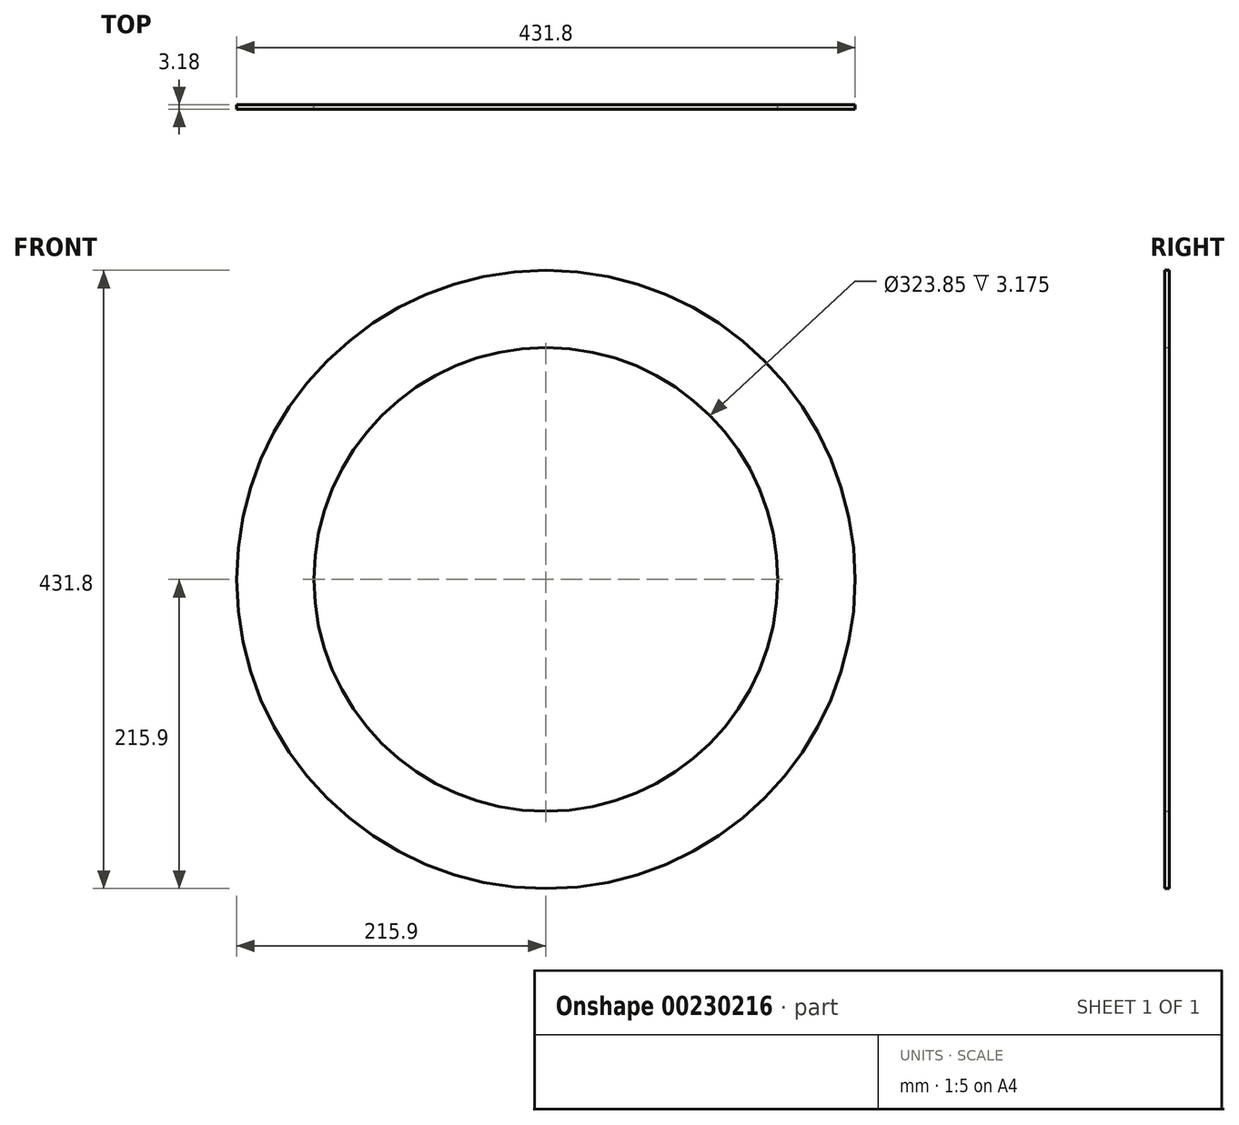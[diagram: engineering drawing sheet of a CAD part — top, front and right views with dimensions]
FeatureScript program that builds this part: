
annotation { "Feature Type Name" : "Feature", "Feature Type Description" : "" }
export const myFeature = defineFeature(function(context is Context, id is Id, definition is map)
    precondition{}
    {
        {
            var Q0;
            Q0=qCreatedBy(makeId("Front.planeOp"),FACE);
            var sketch = newSketch(context, id + "F0", { "sketchPlane" : qUnion([Q0])});
            skCircle(sketch, "E0", {"center": v(0, 0) * mm, "radius": 161.93 * mm});
            skCircle(sketch, "E1", {"center": v(0, 0) * mm, "radius": 215.9 * mm});
            skSolve(sketch);
        }
        {
            var Q0;
            Q0 = qSketchRegion(id + "F0", true);
            extrude(context, id + "F1", {"entities" : qUnion([Q0]), "depth" : 3.17 * mm});
        }
    });
